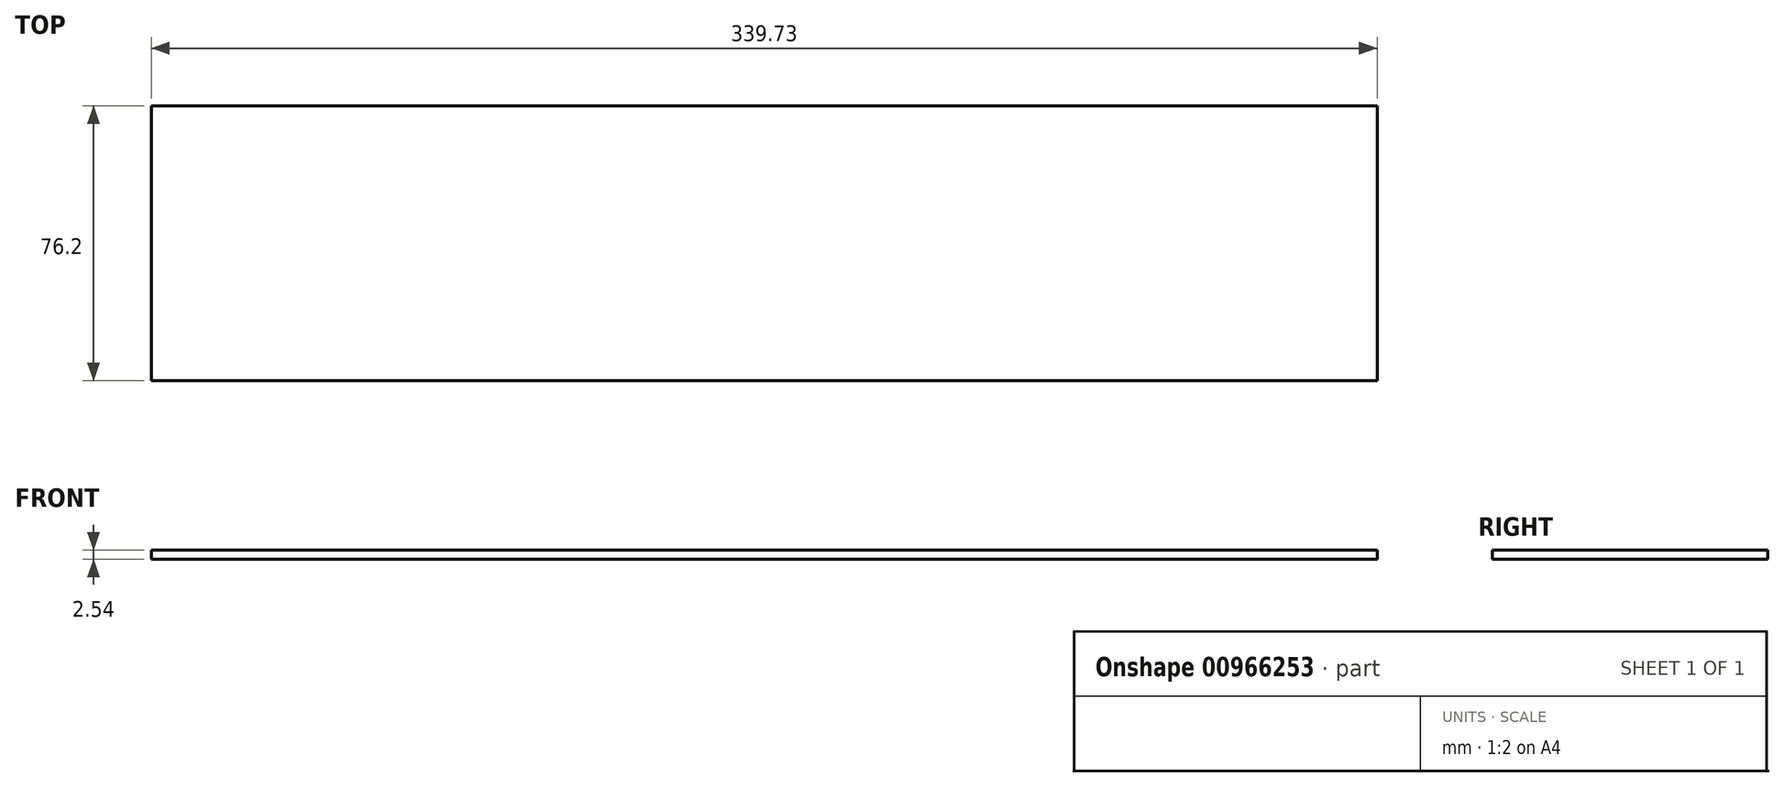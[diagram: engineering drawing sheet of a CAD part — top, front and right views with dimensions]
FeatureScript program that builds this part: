
annotation { "Feature Type Name" : "Feature", "Feature Type Description" : "" }
export const myFeature = defineFeature(function(context is Context, id is Id, definition is map)
    precondition{}
    {
        {
            var Q0;
            Q0=qCreatedBy(makeId("Top.planeOp"),FACE);
            var sketch = newSketch(context, id + "F0", { "sketchPlane" : qUnion([Q0])});
            skLineSegment(sketch, "E0.bottom", {"start": v(0, 0) * mm, "end": v(339.73, 0) * mm});
            skLineSegment(sketch, "E0.top", {"start": v(0, -76.2) * mm, "end": v(339.73, -76.2) * mm});
            skLineSegment(sketch, "E0.right", {"start": v(339.73, 0) * mm, "end": v(339.73, -76.2) * mm});
            skPoint(sketch, "E1.MirrorP", {"position": v(339.73, -50.8) * mm});
            skLineSegment(sketch, "E2", {"start": v(0, 0) * mm, "end": v(0, -76.2) * mm});
            skPoint(sketch, "E3.end.orphan", {"position": v(169.86, 0) * mm});
            skPoint(sketch, "E3.start.orphan", {"position": v(169.86, -76.2) * mm});
            skSolve(sketch);
        }
        {
            var Q0;
            {var subQ0=sQuery(id+"F0.wireOp",EDGE,"E0.left");Q0=makeQuery(id+"F0.imprint","IMPRINT",FACE,{"disambiguationData":[TD([[makeQuery(id+"F0.imprint","IMPRINT",EDGE,{"derivedFrom":subQ0}),1.0]])]});}
            var Q1;
            {var subQ1=sQuery(id+"F0.wireOp",EDGE,"E0.right");Q1=makeQuery(id+"F0.imprint","IMPRINT",FACE,{"disambiguationData":[TD([[makeQuery(id+"F0.imprint","IMPRINT",EDGE,{"derivedFrom":subQ1}),-1.0]])]});}
            var Q2;
            {var subQ2=sQuery(id+"F0.wireOp",EDGE,"E3");Q2=makeQuery(id+"F0.imprint","IMPRINT",FACE,{"disambiguationData":[TD([[makeQuery(id+"F0.imprint","IMPRINT",EDGE,{"derivedFrom":subQ2}),1.0]])]});}
            extrude(context, id + "F1", {"entities" : qUnion([Q0, Q1, Q2]), "depth" : 2.54 * mm});
        }
    });
